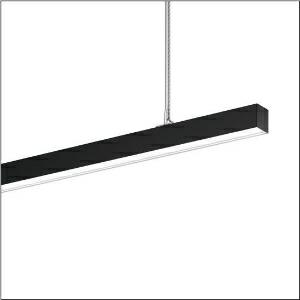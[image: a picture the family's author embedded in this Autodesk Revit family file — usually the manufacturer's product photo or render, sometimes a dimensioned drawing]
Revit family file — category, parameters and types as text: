
# Revit family: silica_r__21_51mx33tctdb_eeca
name_source: partatom
category: Lighting Fixtures
units: mm (PartAtom-declared; Revit-internal decimal feet)

## family parameters
Cut with Voids When Loaded = No
Host = Face
Light Source = No
Part Type = Normal
Room Calculation Point = No
Round Connector Dimension = Use Diameter
Shared = No

## types (1)
- --- (1 x LED, 14340 lm, 134.7 W, 6500K)
    Apparent Load = 135 VA
    CIE Flux Codes = 78 96 99 56 100
    Color Rendering = 80
    Color Temperature = 6500K
    Default Elevation = 1800 mm
    Description = Silica® 21, office luminaire, primary optical cover: prismatic diffuser, of PMMA, CAT 2 (L<= 3000cd/m²), light emission: direct/indirect distribution, primary light characteristic: symmetric, installation type: suspended mounting, LED, rated luminous flux: 14.340lm, luminous efficacy: 101lm/W, light colour: 8tw, colour temperature: 2700..6500K, control gear: DALI DT8, with terminal, 3+2-pole, max. 2.5mm², mains connection: 220..240V, AC, 50/60Hz, rated input power: 141.4W, luminaire housing, of aluminium, matt jet black (RAL 9005), length: 3.004mm, width: 53mm, height: 53mm, protection rating (complete): IP20, insulation class (complete): insulation class I (protective earthing), certification: CE, permissible operating ambient temperature: 0..+35°C, standard: EN 50419, packaging unit: 1 piece
    Height = 53 mm
    Lamp = 1 x LED
    Lamp Light Flux = 14340 lm
    Lamp Power = 134.7 W
    Lamp count = 1
    Length = 3004 mm
    Luminous efficacy = 106 lm/W
    Manufacturer = Siteco
    ModVariant = No
    Model = 51MX33TCTDB
    Mounting Place = Ceiling
    Mounting Type = Pendant
    Number of Poles = 1
    OnlyDefault = Yes
    Power Factor = 1
    Product Name = Silica® 21
    Product group = office luminaire | ceiling pendant
    ProductGroupID = 904
    Protection Class = Protection class I
    Protection Degree = IP 20
    RLX_Detail_Level = 1
    RLX_Emergency_Light_Flux = 0 lm
    RLX_Emergency_Type = 0
    RLX_Emergency_Type_DB = No
    RlxData = <blob elided: 22805 chars, md5=957123bd>
    Socket = socket
    Standby Power = 0 W
    System Light Flux = 14340 lm
    System Power = 135 W
    Type Comments = individual setting
    Type Image = l_1335856.jpg
    URL = http://relux.com
    VarID = @adj_139752
    Voltage = 0 V
    Weight = 0.00 kg
    Width = 53 mm

## geometry (parser evidence)
native form markers: Blend x4, Sweep x12
no freeform markers — native parametric forms only
